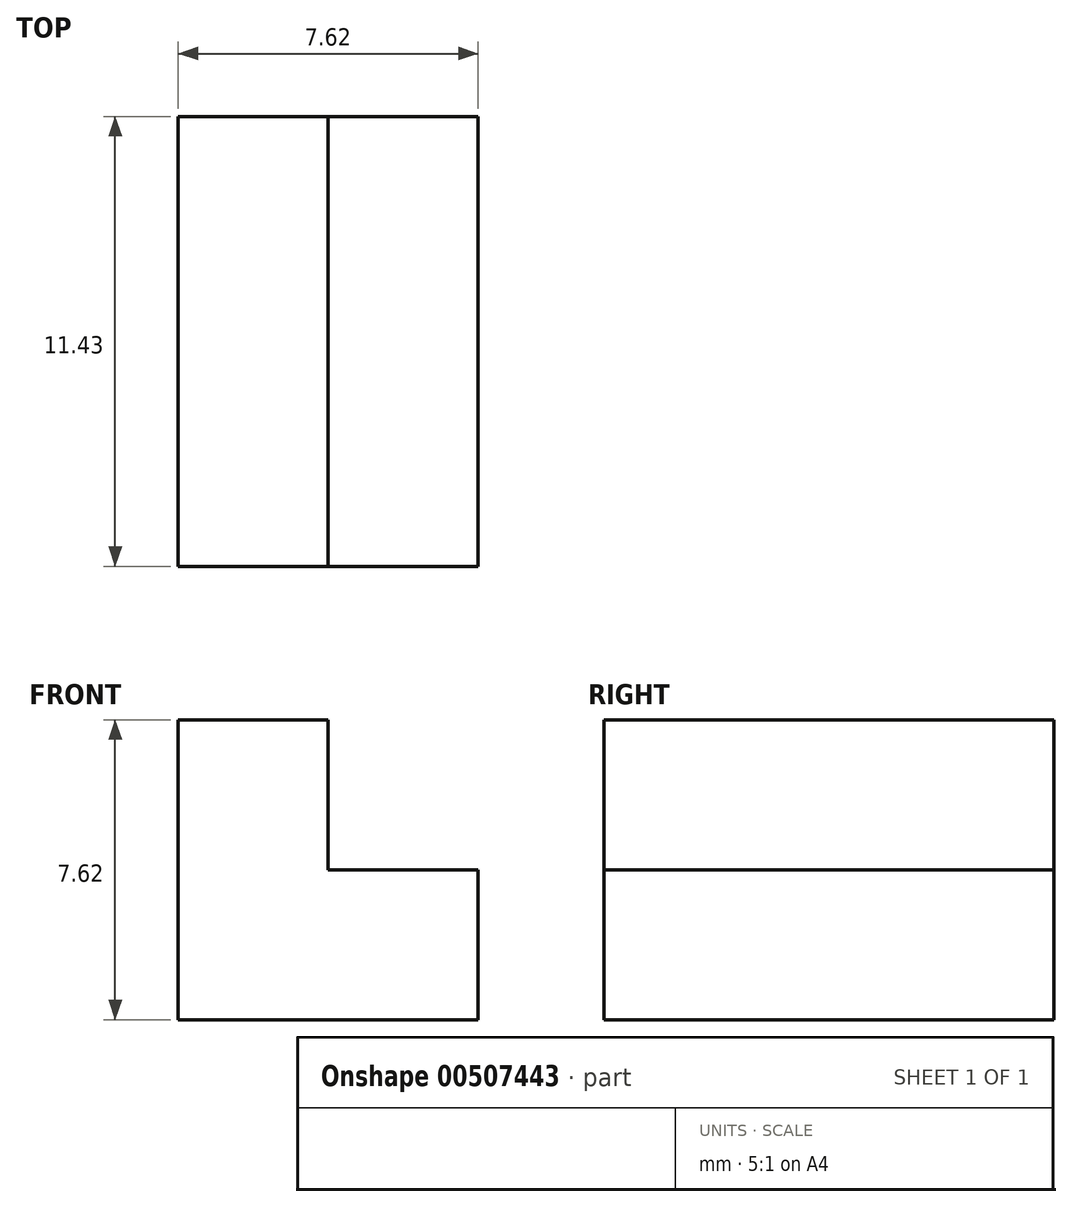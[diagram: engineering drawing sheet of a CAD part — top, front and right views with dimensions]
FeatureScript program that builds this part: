
annotation { "Feature Type Name" : "Feature", "Feature Type Description" : "" }
export const myFeature = defineFeature(function(context is Context, id is Id, definition is map)
    precondition{}
    {
        {
            var Q0;
            Q0=qCreatedBy(makeId("Front.planeOp"),FACE);
            var sketch = newSketch(context, id + "F0", { "sketchPlane" : qUnion([Q0])});
            skLineSegment(sketch, "E0", {"start": v(0, 0) * mm, "end": v(0, 7.62) * mm});
            skLineSegment(sketch, "E1", {"start": v(0, 7.62) * mm, "end": v(3.8, 7.62) * mm});
            skLineSegment(sketch, "E2", {"start": v(3.8, 7.62) * mm, "end": v(3.81, 3.8) * mm});
            skLineSegment(sketch, "E3", {"start": v(3.81, 3.8) * mm, "end": v(7.62, 3.81) * mm});
            skLineSegment(sketch, "E4", {"start": v(7.62, 3.81) * mm, "end": v(7.62, 0) * mm});
            skLineSegment(sketch, "E5", {"start": v(0, 0) * mm, "end": v(7.62, 0) * mm});
            skSolve(sketch);
        }
        {
            var Q0;
            Q0 = qSketchRegion(id + "F0", true);
            extrude(context, id + "F1", {"entities" : qUnion([Q0]), "depth" : 11.43 * mm});
        }
    });
